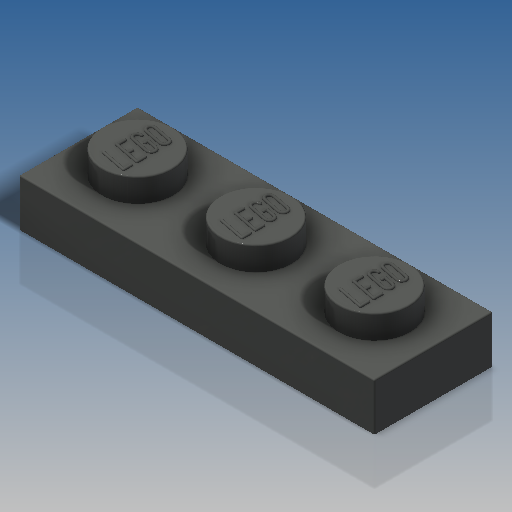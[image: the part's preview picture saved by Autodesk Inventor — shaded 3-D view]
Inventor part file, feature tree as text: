
AUTODESK INVENTOR PART (.ipt)
format: ipt  version: 2019.4 (Build 234330000, 330)  size: 4,584,960 bytes
history: native  units: in
note: dims shown in document units (in); Inventor stores cm internally (conversion verified against a paired STEP export)
features: extrude x4, sketch x4, fillet x2, pattern_linear x2, other x1
ambient origin geometry x8: Origin, YZ Plane, XZ Plane, XY Plane, X Axis, Y Axis, Z Axis, Center Point
bodies: Solid1 (feature_tree)
feature tree (13):
  extrude  "Extrusion1"  Depth=0.315in
  extrude  "Extrusion4"  Depth=0.063in
  other  "LEGO:1"
  fillet  "Fillet2"  Radius=0.063in
  pattern_linear  "Rectangular Pattern1"  Spacing1=0.189in  [1 undecoded]
  sketch  "Sketch3"  dims[d4=0.126in d5=0.0in d7=0.0591in d8=0.063in d11=0.063in d12=0.0in]
  extrude  "Extrusion2"  Depth=0.063in
  extrude  "Extrusion5"  Depth=0.189in
  pattern_linear  "Rectangular Pattern2"  Spacing1=0.1575in  [1 undecoded]
  fillet  "Fillet1"  Radius=0.1575in
  sketch  "Sketch2"  dims[d0=0.9449in d1=0.315in]
  sketch  "Sketch9"  dims[d22=0.0039in]
  sketch  "Sketch10"  dims[d60=0.2564in d61=0.189in d62=0.063in d63=0.189in d64=0.1575in d65=0.1575in d66=0.063in d67=0.0in d68=0.0039in d69=1.1811in d71=0.315in d72=0.3937in d74=0.315in d75=0.315in d76=0.315in d77=0.0709in d78=0.0in d79=0.7874in d81=0.315in d82=0.3937in d84=0.315in d85=0.126in d86=0.0in d87=0.0in d88=0.0in d89=0.0in d90=0.0in d91=0.0079in d92=0.0732in d93=0.0281in d94=0.035in d95=0.0079in d96=0.0139in d97=0.0281in d98=0.035in d99=0.0281in d100=0.0159in d101=0.0177in d102=0.035in d103=0.5428in]
note: 2 required parameter values undecoded (feature->parameter linkage not recoverable at this tier; creation-order binding heuristic only, values carry confidence <= 0.55)
